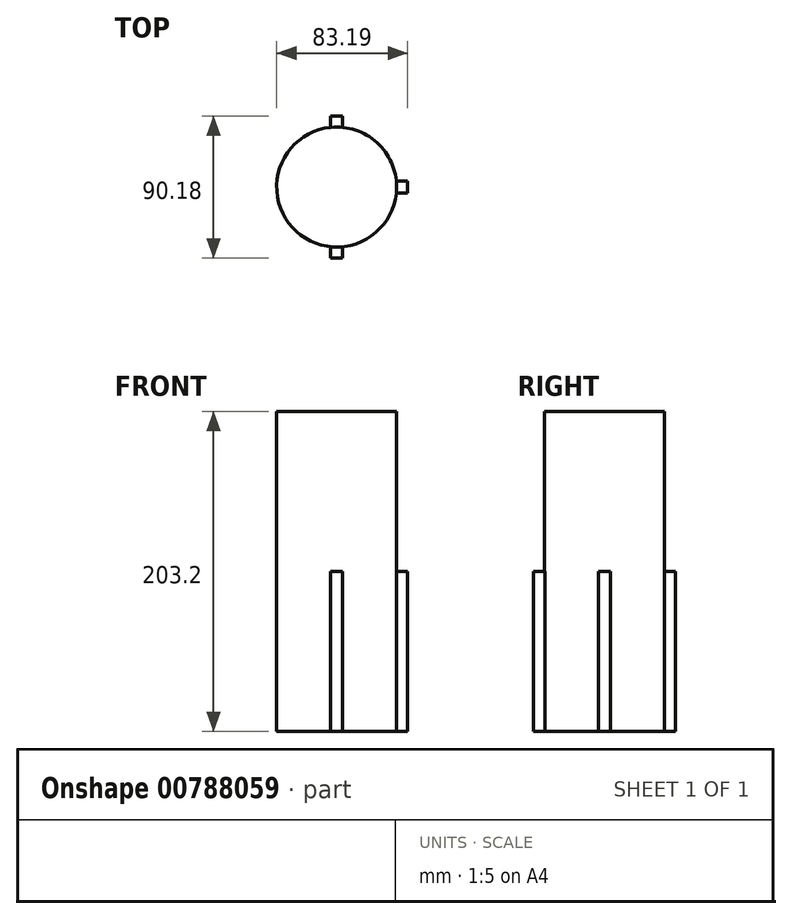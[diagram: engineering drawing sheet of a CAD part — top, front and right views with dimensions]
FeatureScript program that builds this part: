
annotation { "Feature Type Name" : "Feature", "Feature Type Description" : "" }
export const myFeature = defineFeature(function(context is Context, id is Id, definition is map)
    precondition{}
    {
        {
            var Q0;
            Q0=qCreatedBy(makeId("Top.planeOp"),FACE);
            var sketch = newSketch(context, id + "F0", { "sketchPlane" : qUnion([Q0])});
            skCircle(sketch, "E0", {"center": v(0, 0) * mm, "radius": 38.1 * mm});
            skPoint(sketch, "E1", {"position": v(-38.1, 0) * mm});
            skLineSegment(sketch, "E2.bottom", {"start": v(-45.09, 3.81) * mm, "end": v(-31.11, 3.81) * mm});
            skLineSegment(sketch, "E2.top", {"start": v(-45.09, -3.8) * mm, "end": v(-31.11, -3.8) * mm});
            skLineSegment(sketch, "E2.left", {"start": v(-45.09, 3.81) * mm, "end": v(-45.09, -3.8) * mm});
            skLineSegment(sketch, "E2.right", {"start": v(-31.11, 3.81) * mm, "end": v(-31.11, -3.8) * mm});
            skLineSegment(sketch, "E3.MirrorCS", {"start": v(31.11, 3.81) * mm, "end": v(31.11, -3.8) * mm});
            skLineSegment(sketch, "E4.MirrorCS", {"start": v(45.09, 3.81) * mm, "end": v(31.11, 3.81) * mm});
            skLineSegment(sketch, "E5.MirrorCS", {"start": v(45.09, -3.8) * mm, "end": v(31.11, -3.8) * mm});
            skLineSegment(sketch, "E6.MirrorCS", {"start": v(45.09, 3.81) * mm, "end": v(45.09, -3.8) * mm});
            skLineSegment(sketch, "E7.MirrorCS", {"start": v(-31.11, -3.81) * mm, "end": v(-31.11, 3.8) * mm});
            skLineSegment(sketch, "E8.MirrorCS", {"start": v(-45.09, 3.8) * mm, "end": v(-31.11, 3.8) * mm});
            skLineSegment(sketch, "E9.MirrorCS", {"start": v(-45.09, -3.81) * mm, "end": v(-31.11, -3.81) * mm});
            skLineSegment(sketch, "E10.MirrorCS", {"start": v(-45.09, -3.81) * mm, "end": v(-45.09, 3.8) * mm});
            skPoint(sketch, "E11", {"position": v(0, 38.1) * mm});
            skLineSegment(sketch, "E12.bottom", {"start": v(-3.8, 45.09) * mm, "end": v(3.81, 45.09) * mm});
            skLineSegment(sketch, "E12.top", {"start": v(-3.81, 31.11) * mm, "end": v(3.8, 31.11) * mm});
            skLineSegment(sketch, "E12.left", {"start": v(-3.8, 45.09) * mm, "end": v(-3.81, 31.11) * mm});
            skLineSegment(sketch, "E12.right", {"start": v(3.81, 45.09) * mm, "end": v(3.8, 31.11) * mm});
            skLineSegment(sketch, "E13.MirrorCS", {"start": v(-3.8, -45.09) * mm, "end": v(-3.81, -31.11) * mm});
            skLineSegment(sketch, "E14.MirrorCS", {"start": v(-3.81, -31.11) * mm, "end": v(3.8, -31.11) * mm});
            skLineSegment(sketch, "E15.MirrorCS", {"start": v(-3.8, -45.09) * mm, "end": v(3.81, -45.09) * mm});
            skLineSegment(sketch, "E16.MirrorCS", {"start": v(3.81, -45.09) * mm, "end": v(3.8, -31.11) * mm});
            skSolve(sketch);
        }
        {
            var Q0;
            {var subQ0=sQuery(id+"F0.wireOp",EDGE,"E3.MirrorCS");Q0=makeQuery(id+"F0.imprint","IMPRINT",FACE,{"disambiguationData":[TD([[makeQuery(id+"F0.imprint","IMPRINT",EDGE,{"derivedFrom":subQ0}),1.0]])]});}
            var Q1;
            {var subQ0=sQuery(id+"F0.wireOp",EDGE,"E2.right");Q1=makeQuery(id+"F0.imprint","IMPRINT",FACE,{"disambiguationData":[TD([[makeQuery(id+"F0.imprint","IMPRINT",EDGE,{"derivedFrom":subQ0}),-1.0]])]});}
            var Q2;
            {var subQ0=sQuery(id+"F0.wireOp",EDGE,"E12.top");Q2=makeQuery(id+"F0.imprint","IMPRINT",FACE,{"disambiguationData":[TD([[makeQuery(id+"F0.imprint","IMPRINT",EDGE,{"derivedFrom":subQ0}),1.0]])]});}
            var Q3;
            {var subQ0=sQuery(id+"F0.wireOp",EDGE,"E14.MirrorCS");Q3=makeQuery(id+"F0.imprint","IMPRINT",FACE,{"disambiguationData":[TD([[makeQuery(id+"F0.imprint","IMPRINT",EDGE,{"derivedFrom":subQ0}),-1.0]])]});}
            var Q4;
            {var subQ12=sQuery(id+"F0.wireOp",EDGE,"E3.MirrorCS");Q4=makeQuery(id+"F0.imprint","IMPRINT",FACE,{"disambiguationData":[TD([[makeQuery(id+"F0.imprint","IMPRINT",EDGE,{"derivedFrom":subQ12}),-1.0]])]});}
            extrude(context, id + "F1", {"entities" : qUnion([Q0, Q1, Q2, Q3, Q4]), "depth" : 203.2 * mm, "offsetDistance" : 25.4 * mm});
        }
        {
            var Q0;
            {var subQ0=sQuery(id+"F0.wireOp",EDGE,"E10.MirrorCS");Q0=makeQuery(id+"F0.imprint","IMPRINT",FACE,{"disambiguationData":[TD([[makeQuery(id+"F0.imprint","IMPRINT",EDGE,{"derivedFrom":subQ0}),-1.0]])]});}
            var Q1;
            {var subQ0=sQuery(id+"F0.wireOp",EDGE,"E15.MirrorCS");Q1=makeQuery(id+"F0.imprint","IMPRINT",FACE,{"disambiguationData":[TD([[makeQuery(id+"F0.imprint","IMPRINT",EDGE,{"derivedFrom":subQ0}),1.0]])]});}
            var Q2;
            {var subQ0=sQuery(id+"F0.wireOp",EDGE,"E6.MirrorCS");Q2=makeQuery(id+"F0.imprint","IMPRINT",FACE,{"disambiguationData":[TD([[makeQuery(id+"F0.imprint","IMPRINT",EDGE,{"derivedFrom":subQ0}),-1.0]])]});}
            var Q3;
            {var subQ0=sQuery(id+"F0.wireOp",EDGE,"E12.bottom");Q3=makeQuery(id+"F0.imprint","IMPRINT",FACE,{"disambiguationData":[TD([[makeQuery(id+"F0.imprint","IMPRINT",EDGE,{"derivedFrom":subQ0}),-1.0]])]});}
            extrude(context, id + "F2", {"entities" : qUnion([Q0, Q1, Q2, Q3]), "operationType" : NewBodyOperationType.ADD, "depth" : 101.6 * mm, "offsetDistance" : 25.4 * mm});
        }
    });
